# Revit family: TSJPRS Series - Swing Joints
name_source: partatom
category: Acessórios do tubo
units: mm (PartAtom-declared; Revit-internal decimal feet)

## family parameters
Com base no plano de trabalho = Não
Compartilhado = Sim
Corte com vazios quando carregada = Não
Cota do conector redondo = Utilizar diâmetro
Número OmniClass = 23.60.30.11.14
Sempre na vertical = Sim
Tipo de parte = Normal
Título OmniClass = Pipework Fittings

## types (3) — shared parameters
Lenght Swing Pipe = 305  [stored 1.00066 ft]
Lookup Table Name = TABELA1
Material = Plastic White
Raio Swing Pipe = 15  [stored 0.0492126 ft]
SupportProjetos: Level of Detail = LOD 300
SupportProjetos: Reviw = R00
x = 12  [stored 0.0393701 ft]
zero-valued in all types: Elevação padrão

## per-type parameters (varying)
| type | Descrição | Modelo | RainBird: Code | RainBird: Description |
| TSJ-12075 | TSJ-12075 - Swing Joints | TSJ-12075 | A66715 | TSJ-12075 - Swing Joints |
| TSJ12 | TSJ-12 - Swing Joints | TSJ-12 | A66705 | TSJ-12 - Swing Joints |
| TSJ100PRS | TSJ-100-PRS - Swing Joints | TSJ100PRS | A66755 | TSJ-100-PRS - Swing Joints |

note: [stored X ft] marks values corroborated as IEEE doubles in the binary element streams (Revit-internal decimal feet)
